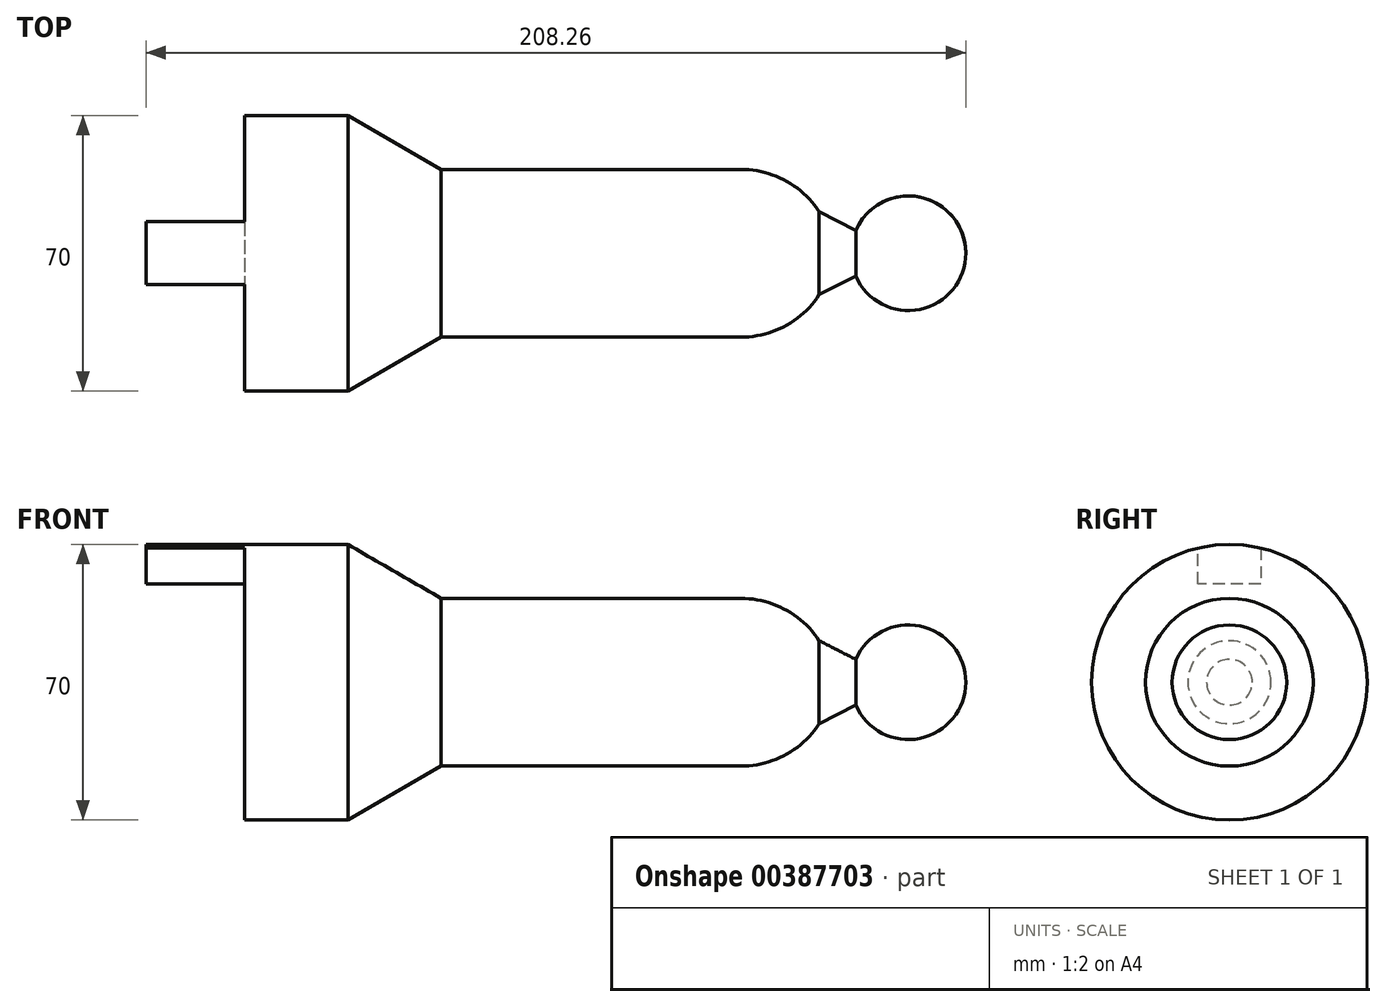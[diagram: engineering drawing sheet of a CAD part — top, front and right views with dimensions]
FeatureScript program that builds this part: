
annotation { "Feature Type Name" : "Feature", "Feature Type Description" : "" }
export const myFeature = defineFeature(function(context is Context, id is Id, definition is map)
    precondition{}
    {
        {
            var Q0;
            Q0=qCreatedBy(makeId("Top.planeOp"),FACE);
            var sketch = newSketch(context, id + "F0", { "sketchPlane" : qUnion([Q0])});
            skLineSegment(sketch, "E0", {"start": v(-52.6, 0) * mm, "end": v(-52.6, 35) * mm});
            skLineSegment(sketch, "E1", {"start": v(-52.6, 35) * mm, "end": v(-26.3, 35) * mm});
            skLineSegment(sketch, "E2", {"start": v(-26.3, 35) * mm, "end": v(-2.6, 21.31) * mm});
            skLineSegment(sketch, "E3", {"start": v(-2.6, 21.31) * mm, "end": v(73.52, 21.31) * mm});
            skArc(sketch, "E4", {"start": v(93.45, 10.55) * mm, "mid": v(84.85, 18.45) * mm, "end": v(73.52, 21.31) * mm});
            skLineSegment(sketch, "E5", {"start": v(-52.6, 0) * mm, "end": v(97.21, 0) * mm});
            skArc(sketch, "E6", {"start": v(130.67, 0) * mm, "mid": v(119.08, 14.26) * mm, "end": v(102.75, 5.8) * mm});
            skLineSegment(sketch, "E7", {"start": v(93.45, 10.55) * mm, "end": v(102.75, 5.8) * mm});
            skLineSegment(sketch, "E8", {"start": v(97.21, 0) * mm, "end": v(130.67, 0) * mm});
            skSolve(sketch);
        }
        {
            var Q0;
            Q0=makeQuery(id+"F0.imprint","IMPRINT",FACE,{"disambiguationData":[TD([[makeQuery(id+"F0.imprint","IMPRINT",EDGE,{"derivedFrom":sQuery(id+"F0.wireOp",EDGE,"E0")}),-1.0]])]});
            var Q1;
            Q1=sQuery(id+"F0.wireOp",EDGE,"E5");
            revolve(context, id + "F1", {"entities" : qUnion([Q0]), "axis" : qUnion([Q1]), "revolveType" : RevolveType.FULL});
        }
        {
            var Q0;
            Q0=makeQuery(id+"F1.opRevolve","SWEPT_FACE",FACE,{"disambiguationData":[OSD([sQuery(id+"F0.wireOp",EDGE,"E0")])]});
            var sketch = newSketch(context, id + "F2", { "sketchPlane" : qUnion([Q0])});
            skLineSegment(sketch, "E9", {"start": v(-8, 34.07) * mm, "end": v(-8, 25) * mm});
            skLineSegment(sketch, "E10", {"start": v(-8, 25) * mm, "end": v(8, 25) * mm});
            skLineSegment(sketch, "E11", {"start": v(8, 25) * mm, "end": v(8, 34.07) * mm});
            skArc(sketch, "E12", {"start": v(8, 34.07) * mm, "mid": v(0, 35) * mm, "end": v(-8, 34.07) * mm});
            skSolve(sketch);
        }
        {
            var Q0;
            Q0 = qSketchRegion(id + "F2", true);
            extrude(context, id + "F3", {"entities" : qUnion([Q0]), "operationType" : NewBodyOperationType.ADD, "depth" : 25 * mm});
        }
    });
